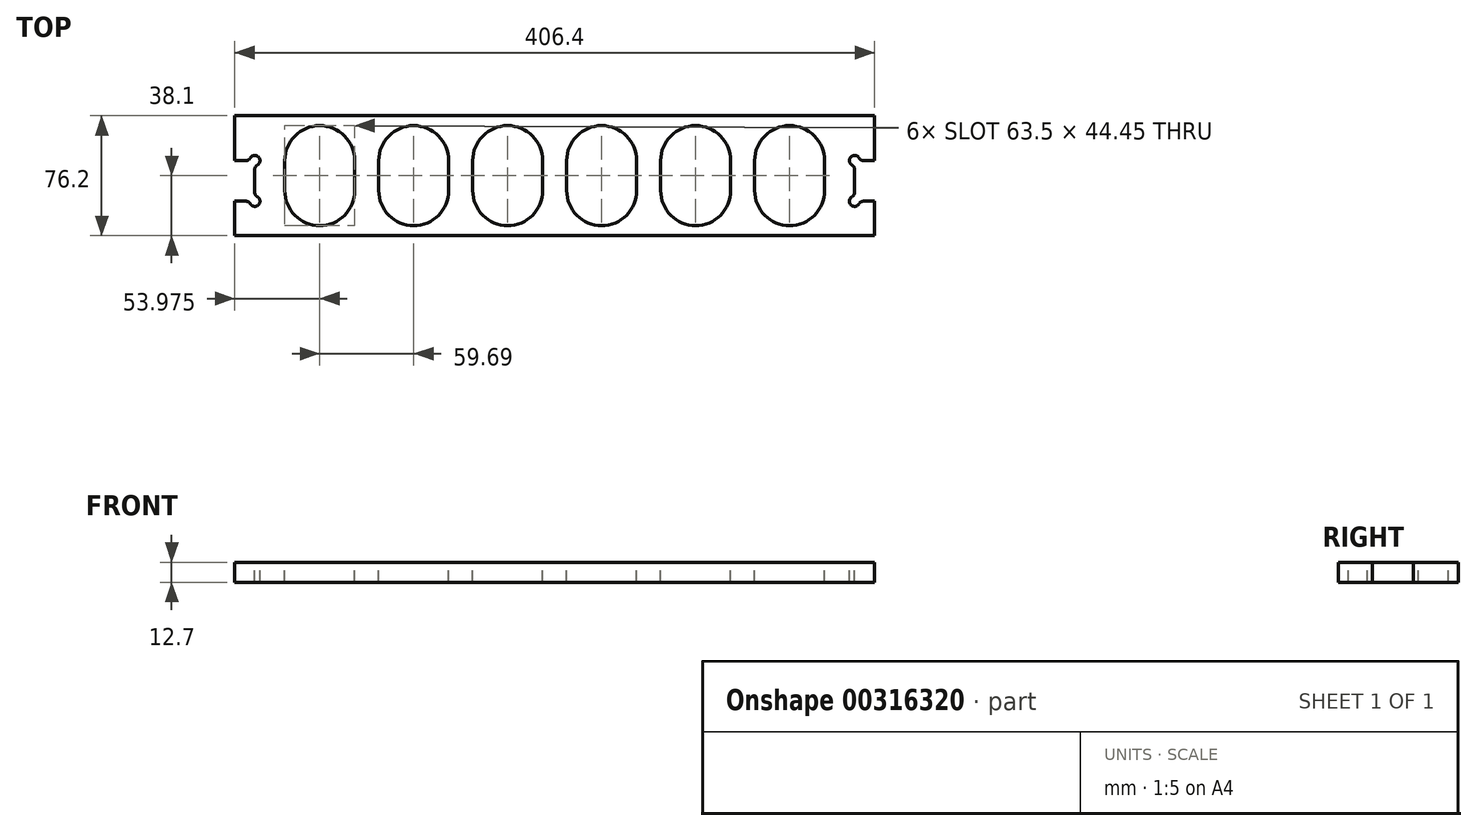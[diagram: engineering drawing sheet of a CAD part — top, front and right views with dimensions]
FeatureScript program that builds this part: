
annotation { "Feature Type Name" : "Feature", "Feature Type Description" : "" }
export const myFeature = defineFeature(function(context is Context, id is Id, definition is map)
    precondition{}
    {
        {
            var Q0;
            Q0=qCreatedBy(makeId("Top.planeOp"),FACE);
            var sketch = newSketch(context, id + "F0", { "sketchPlane" : qUnion([Q0])});
            skLineSegment(sketch, "E0.bottom", {"start": v(0, 0) * mm, "end": v(406.4, 0) * mm});
            skLineSegment(sketch, "E0.top", {"start": v(0, 76.2) * mm, "end": v(406.4, 76.2) * mm});
            skLineSegment(sketch, "E0.left", {"start": v(0, 0) * mm, "end": v(0, 76.2) * mm});
            skLineSegment(sketch, "E0.right", {"start": v(406.4, 0) * mm, "end": v(406.4, 76.2) * mm});
            skSolve(sketch);
        }
        {
            var Q0;
            Q0=qSketchRegion(id+"F0",true);
            extrude(context, id + "F1", {"entities" : qUnion([Q0]), "depth" : 12.7 * mm});
        }
        {
            var Q0;
            Q0=makeQuery(id+"F1.opExtrude","CAP_FACE",FACE,{"disambiguationData":[OSD([sQuery(id+"F0.wireOp",EDGE,"E0.bottom"),sQuery(id+"F0.wireOp",EDGE,"E0.top"),sQuery(id+"F0.wireOp",EDGE,"E0.left"),sQuery(id+"F0.wireOp",EDGE,"E0.right")])],"isStart":false});
            var sketch = newSketch(context, id + "F2", { "sketchPlane" : qUnion([Q0])});
            skLineSegment(sketch, "E1", {"start": v(0, 38.1) * mm, "end": v(103.18, 38.1) * mm, "construction": true});
            skLineSegment(sketch, "E2", {"start": v(203.2, 76.2) * mm, "end": v(203.2, 0) * mm, "construction": true});
            skLineSegment(sketch, "E3.bottom", {"start": v(0, 47.63) * mm, "end": v(7.05, 47.63) * mm});
            skLineSegment(sketch, "E3.top", {"start": v(0, 21.84) * mm, "end": v(7.05, 21.84) * mm});
            skLineSegment(sketch, "E3.left", {"start": v(0, 47.63) * mm, "end": v(0, 21.84) * mm});
            skLineSegment(sketch, "E3.right", {"start": v(12.7, 41.98) * mm, "end": v(12.7, 27.49) * mm});
            skArc(sketch, "E4", {"start": v(14.32, 44.75) * mm, "mid": v(15.03, 49.96) * mm, "end": v(9.82, 49.24) * mm});
            skArc(sketch, "E5", {"start": v(9.82, 20.23) * mm, "mid": v(15.03, 19.5) * mm, "end": v(14.32, 24.72) * mm});
            skPoint(sketch, "E6.visualSharp", {"position": v(9.4, 47.63) * mm});
            skArc(sketch, "E6.filletArc", {"start": v(7.05, 47.63) * mm, "mid": v(8.66, 48.06) * mm, "end": v(9.82, 49.24) * mm});
            skPoint(sketch, "E7.visualSharp", {"position": v(9.4, 21.84) * mm});
            skArc(sketch, "E7.filletArc", {"start": v(9.82, 20.23) * mm, "mid": v(8.66, 21.4) * mm, "end": v(7.05, 21.84) * mm});
            skPoint(sketch, "E8.visualSharp", {"position": v(12.7, 44.32) * mm});
            skArc(sketch, "E8.filletArc", {"start": v(14.32, 44.75) * mm, "mid": v(13.13, 43.58) * mm, "end": v(12.7, 41.98) * mm});
            skPoint(sketch, "E9.visualSharp", {"position": v(12.7, 25.15) * mm});
            skArc(sketch, "E9.filletArc", {"start": v(12.7, 27.49) * mm, "mid": v(13.13, 25.89) * mm, "end": v(14.32, 24.72) * mm});
            skArc(sketch, "E10.MirrorCS", {"start": v(393.7, 27.49) * mm, "mid": v(393.27, 25.89) * mm, "end": v(392.08, 24.72) * mm});
            skArc(sketch, "E11.MirrorCS", {"start": v(399.35, 47.63) * mm, "mid": v(397.74, 48.06) * mm, "end": v(396.58, 49.24) * mm});
            skArc(sketch, "E12.MirrorCS", {"start": v(392.08, 44.75) * mm, "mid": v(391.37, 49.96) * mm, "end": v(396.58, 49.24) * mm});
            skLineSegment(sketch, "E13.MirrorCS", {"start": v(406.4, 47.63) * mm, "end": v(399.35, 47.63) * mm});
            skArc(sketch, "E14.MirrorCS", {"start": v(396.58, 20.23) * mm, "mid": v(397.74, 21.4) * mm, "end": v(399.35, 21.84) * mm});
            skArc(sketch, "E15.MirrorCS", {"start": v(392.08, 44.75) * mm, "mid": v(393.27, 43.58) * mm, "end": v(393.7, 41.98) * mm});
            skLineSegment(sketch, "E16.MirrorCS", {"start": v(406.4, 21.84) * mm, "end": v(399.35, 21.84) * mm});
            skPoint(sketch, "E17.MirrorP", {"position": v(397, 47.63) * mm});
            skPoint(sketch, "E18.MirrorP", {"position": v(393.7, 25.15) * mm});
            skArc(sketch, "E19.MirrorCS", {"start": v(396.58, 20.23) * mm, "mid": v(391.37, 19.5) * mm, "end": v(392.08, 24.72) * mm});
            skPoint(sketch, "E20.MirrorP", {"position": v(393.7, 44.32) * mm});
            skPoint(sketch, "E21.MirrorP", {"position": v(397, 21.84) * mm});
            skLineSegment(sketch, "E22.MirrorCS", {"start": v(393.7, 41.98) * mm, "end": v(393.7, 27.49) * mm});
            skLineSegment(sketch, "E23.MirrorCS", {"start": v(406.4, 47.63) * mm, "end": v(406.4, 21.84) * mm});
            skSolve(sketch);
        }
        {
            var Q0;
            Q0=qSketchRegion(id+"F2",true);
            extrude(context, id + "F3", {"entities" : qUnion([Q0]), "operationType" : NewBodyOperationType.REMOVE, "oppositeDirection" : true, "depth" : 25.4 * mm});
        }
        {
            var Q0;
            Q0=makeQuery(id+"F1.opExtrude","CAP_FACE",FACE,{"disambiguationData":[OSD([sQuery(id+"F0.wireOp",EDGE,"E0.bottom"),sQuery(id+"F0.wireOp",EDGE,"E0.top"),sQuery(id+"F0.wireOp",EDGE,"E0.left"),sQuery(id+"F0.wireOp",EDGE,"E0.right")])],"isStart":false});
            var sketch = newSketch(context, id + "F4", { "sketchPlane" : qUnion([Q0])});
            skLineSegment(sketch, "E24", {"start": v(203.2, 76.2) * mm, "end": v(203.2, 0) * mm, "construction": true});
            skLineSegment(sketch, "E25", {"start": v(203.2, 38.1) * mm, "end": v(12.7, 38.1) * mm, "construction": true});
            skLineSegment(sketch, "E26.left", {"start": v(76.2, 28.57) * mm, "end": v(76.2, 47.62) * mm});
            skLineSegment(sketch, "E26.right", {"start": v(31.75, 28.57) * mm, "end": v(31.75, 47.62) * mm});
            skPoint(sketch, "E26.middle", {"position": v(53.97, 38.1) * mm});
            skArc(sketch, "E27", {"start": v(76.2, 47.62) * mm, "mid": v(53.97, 69.85) * mm, "end": v(31.75, 47.62) * mm});
            skArc(sketch, "E28", {"start": v(31.75, 28.57) * mm, "mid": v(53.98, 6.35) * mm, "end": v(76.2, 28.57) * mm});
            skLineSegment(sketch, "E29.1.0.0", {"start": v(91.44, 28.57) * mm, "end": v(91.44, 47.62) * mm});
            skPoint(sketch, "E29.1.0.1", {"position": v(113.66, 38.1) * mm});
            skLineSegment(sketch, "E29.1.0.2", {"start": v(135.9, 28.57) * mm, "end": v(135.9, 47.62) * mm});
            skArc(sketch, "E29.1.0.3", {"start": v(135.89, 47.62) * mm, "mid": v(113.66, 69.85) * mm, "end": v(91.44, 47.62) * mm});
            skArc(sketch, "E29.1.0.4", {"start": v(91.44, 28.57) * mm, "mid": v(113.67, 6.35) * mm, "end": v(135.89, 28.57) * mm});
            skLineSegment(sketch, "E29.2.0.0", {"start": v(151.13, 28.57) * mm, "end": v(151.13, 47.62) * mm});
            skPoint(sketch, "E29.2.0.1", {"position": v(173.35, 38.1) * mm});
            skLineSegment(sketch, "E29.2.0.2", {"start": v(195.58, 28.57) * mm, "end": v(195.58, 47.62) * mm});
            skArc(sketch, "E29.2.0.3", {"start": v(195.58, 47.62) * mm, "mid": v(173.35, 69.85) * mm, "end": v(151.13, 47.62) * mm});
            skArc(sketch, "E29.2.0.4", {"start": v(151.13, 28.57) * mm, "mid": v(173.36, 6.35) * mm, "end": v(195.58, 28.57) * mm});
            skLineSegment(sketch, "E29.3.0.0", {"start": v(210.82, 28.57) * mm, "end": v(210.82, 47.62) * mm});
            skPoint(sketch, "E29.3.0.1", {"position": v(233.05, 38.1) * mm});
            skLineSegment(sketch, "E29.3.0.2", {"start": v(255.27, 28.57) * mm, "end": v(255.27, 47.62) * mm});
            skArc(sketch, "E29.3.0.3", {"start": v(255.27, 47.62) * mm, "mid": v(233.04, 69.85) * mm, "end": v(210.82, 47.62) * mm});
            skArc(sketch, "E29.3.0.4", {"start": v(210.82, 28.57) * mm, "mid": v(233.05, 6.35) * mm, "end": v(255.27, 28.57) * mm});
            skLineSegment(sketch, "E29.4.0.0", {"start": v(270.51, 28.57) * mm, "end": v(270.51, 47.62) * mm});
            skPoint(sketch, "E29.4.0.1", {"position": v(292.74, 38.1) * mm});
            skLineSegment(sketch, "E29.4.0.2", {"start": v(314.96, 28.57) * mm, "end": v(314.96, 47.62) * mm});
            skArc(sketch, "E29.4.0.3", {"start": v(314.96, 47.62) * mm, "mid": v(292.73, 69.85) * mm, "end": v(270.5, 47.62) * mm});
            skArc(sketch, "E29.4.0.4", {"start": v(270.51, 28.57) * mm, "mid": v(292.74, 6.35) * mm, "end": v(314.96, 28.57) * mm});
            skLineSegment(sketch, "E29.5.0.0", {"start": v(330.2, 28.57) * mm, "end": v(330.2, 47.62) * mm});
            skPoint(sketch, "E29.5.0.1", {"position": v(352.43, 38.1) * mm});
            skLineSegment(sketch, "E29.5.0.2", {"start": v(374.65, 28.57) * mm, "end": v(374.65, 47.62) * mm});
            skArc(sketch, "E29.5.0.3", {"start": v(374.65, 47.62) * mm, "mid": v(352.43, 69.85) * mm, "end": v(330.2, 47.62) * mm});
            skArc(sketch, "E29.5.0.4", {"start": v(330.2, 28.57) * mm, "mid": v(352.43, 6.35) * mm, "end": v(374.65, 28.57) * mm});
            skLineSegment(sketch, "E29.direction1", {"start": v(31.75, 28.57) * mm, "end": v(91.44, 28.57) * mm, "construction": true});
            skSolve(sketch);
        }
        {
            var Q0;
            Q0=qSketchRegion(id+"F4",true);
            extrude(context, id + "F5", {"entities" : qUnion([Q0]), "operationType" : NewBodyOperationType.REMOVE, "oppositeDirection" : true, "depth" : 25.4 * mm});
        }
    });
